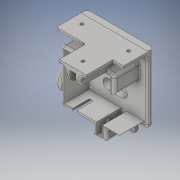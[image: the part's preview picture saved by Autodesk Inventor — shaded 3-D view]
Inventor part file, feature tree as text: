
AUTODESK INVENTOR PART (.ipt)
format: ipt  version: 2016 (Build 200138000, 138)  size: 1,123,328 bytes
history: native  units: in
note: dims shown in document units (in); Inventor stores cm internally (conversion verified against a paired STEP export)
features: fillet x19, sketch x18, extrude x14, plane x5, hole x3
ambient origin geometry x8: Origin, YZ Plane, XZ Plane, XY Plane, X Axis, Y Axis, Z Axis, Center Point
bodies: Solid1 (feature_tree)
feature tree (59):
  extrude  "Extrusion1"  Depth=0.8976in
  sketch  "Sketch12"  dims[d11=0.0787in d12=0.0787in d13=0.0787in d14=0.0787in d82=0.9016in d83=0.8858in]
  plane  "Work Plane6"
  extrude  "Extrusion5"  Depth=0.9016in
  plane  "Work Plane5"
  hole  "Hole3"  [1 undecoded]
  plane  "Work Plane1"
  extrude  "Extrusion6"  Depth=0.6142in
  extrude  "Extrusion7"  Depth=0.1614in
  plane  "Work Plane4"
  extrude  "Extrusion8"  Depth=0.2165in
  fillet  "Fillet15"  Radius=0.2165in
  plane  "Work Plane3"
  extrude  "Extrusion10"  Depth=0.0787in
  extrude  "Extrusion12"  Depth=0.0787in
  extrude  "Extrusion13"  Depth=0.0787in
  hole  "Hole4"  [1 undecoded]
  extrude  "Extrusion14"  Depth=0.0394in
  extrude  "Extrusion15"  Depth=0.0394in
  fillet  "Fillet19"  Radius=0.1575in
  fillet  "Fillet20"  Radius=0.0787in
  fillet  "Fillet22"  Radius=0.0787in
  fillet  "Fillet23"  Radius=0.0394in
  fillet  "Fillet24"  Radius=0.9016in
  fillet  "Fillet26"  Radius=0.1378in
  sketch  "Sketch37"  dims[d133=0.2165in d136=0.0787in]
  fillet  "Fillet29"  Radius=0.185in
  fillet  "Fillet30"  Radius=0.3543in
  extrude  "Extrusion16"  Depth=0.0787in
  hole  "Hole5"  [1 undecoded]
  extrude  "Extrusion18"  Depth=0.7461in
  fillet  "Fillet33"  Radius=0.0394in
  fillet  "Fillet36"  Radius=0.2717in
  fillet  "Fillet38"  Radius=0.2323in
  fillet  "Fillet39"  Radius=0.2835in
  fillet  "Fillet40"  Radius=0.4016in
  extrude  "Extrusion19"  Depth=0.3937in TaperAngle=0.0deg
  fillet  "Fillet41"  Radius=0.0787in
  fillet  "Fillet42"  Radius=0.0669in
  fillet  "Fillet43"  Radius=0.0906in
  extrude  "Extrusion20"  Depth=0.0787in
  fillet  "Fillet44"  Radius=0.1772in
  fillet  "Fillet45"  Radius=0.0483in
  sketch  "Sketch1"  dims[d2=0.1181in d3=0.0in d6=0.8976in d9=0.357in d10=0.7139in]
  sketch  "Sketch14"  dims[d85=0.1102in d86=0.1102in]
  sketch  "Sketch17"  dims[d87=0.6142in d88=0.6142in]
  sketch  "Sketch18"  dims[d89=0.1614in d90=0.1614in]
  sketch  "Sketch22"  dims[d91=0.2992in d92=0.2165in d93=0.2165in]
  sketch  "Sketch24"  dims[d95=0.9016in d97=0.0787in]
  sketch  "Sketch30"  dims[d98=0.0787in d100=0.0787in]
  sketch  "Sketch32"  dims[d101=0.0787in d102=0.0787in]
  sketch  "Sketch33"  dims[d103=0.1693in d105=0.0787in]
  sketch  "Sketch35"  dims[d106=0.0394in d107=0.0394in]
  sketch  "Sketch36"  dims[d108=0.0394in d109=0.0394in d110=0.1575in d111=0.0787in d112=0.0787in d113=0.0394in d114=0.9016in d125=0.1378in d130=0.185in d132=0.3543in]
  sketch  "Sketch38"  dims[d137=0.315in d138=0.0in d139=0.0394in]
  sketch  "Sketch40"  dims[d144=0.0394in d145=0.7461in d146=0.0394in]
  sketch  "Sketch41"  dims[d147=0.07in d148=0.2362in d149=0.119in d150=0.0787in d151=0.5635in d152=0.315in d153=0.8108in d156=0.2717in d157=0.2323in d158=0.2835in d159=0.4016in]
  sketch  "Sketch42"  dims[d160=0.1575in d161=0.0in d164=0.3937in d165=0.0in d166=0.0787in d167=0.0in d171=0.0669in d177=0.0906in d178=0.0in]
  sketch  "Sketch43"  dims[d181=0.0787in d182=0.0787in d185=0.1772in d186=0.0483in d187=0.1063in d188=0.4724in d189=0.0in d190=0.3135in d191=0.4724in d192=0.0in d194=0.2559in d195=0.0394in d196=0.2559in d197=0.0394in d198=0.0787in d199=0.2362in d200=0.1575in d201=0.0787in d202=90.0deg d203=0.315in d204=0.8108in d205=0.1575in d206=0.0in d207=0.0394in d208=0.3937in d209=0.0in d210=0.0787in d211=0.0787in d213=0.0787in d214=0.0591in d215=0.0591in d217=0.0157in d220=0.0591in d221=0.0591in d222=0.5197in d223=0.126in d224=0.126in d225=0.5118in d226=0.0in d236=0.2953in d237=0.1969in d238=0.2953in d239=0.1969in d240=0.2953in d241=0.2953in d242=0.1969in d243=0.2598in d244=0.2598in d245=0.0591in d246=0.2362in d247=0.1575in d248=0.0787in d249=90.0deg d250=0.1181in d251=0.8108in d252=0.0197in d253=0.0in d254=0.0787in d257=0.0591in d259=0.0512in d260=0.0512in d261=0.0512in d262=0.5118in d263=0.0in d264=0.0984in d265=0.0394in d266=0.1181in d267=0.1969in d268=0.1969in d269=0.1575in d270=0.1575in d271=0.3937in d272=0.0in d273=0.0394in d274=0.0197in d26=0.0394in d27=0.0394in]
note: 3 required parameter values undecoded (feature->parameter linkage not recoverable at this tier; creation-order binding heuristic only, values carry confidence <= 0.55)
